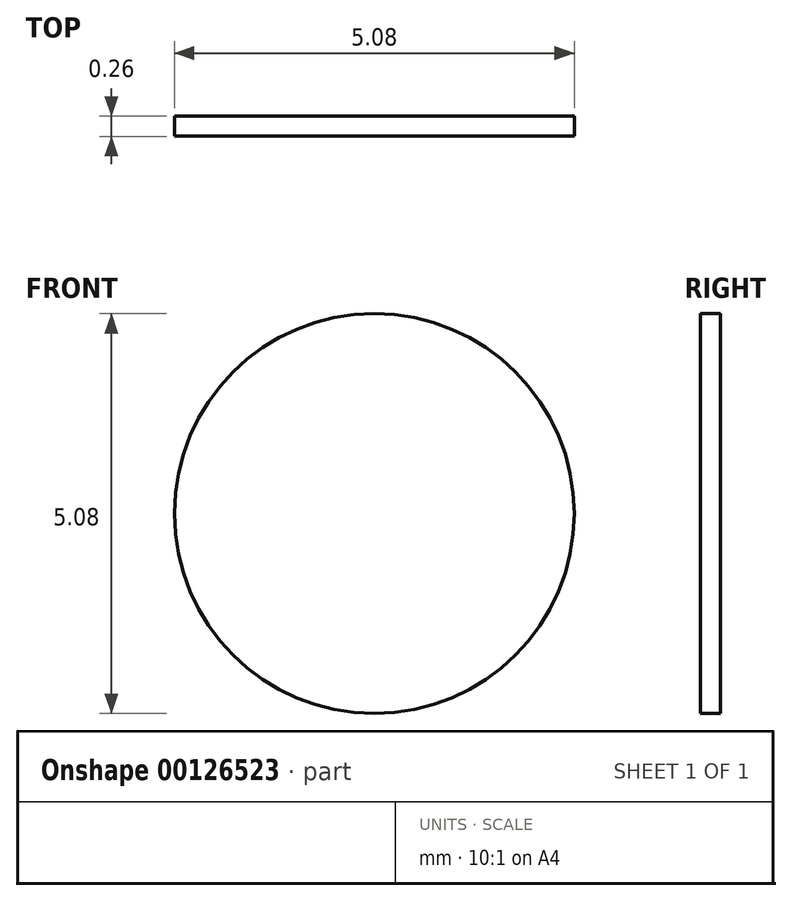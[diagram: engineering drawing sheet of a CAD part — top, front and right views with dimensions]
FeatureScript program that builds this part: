
annotation { "Feature Type Name" : "Feature", "Feature Type Description" : "" }
export const myFeature = defineFeature(function(context is Context, id is Id, definition is map)
    precondition{}
    {
        {
            var Q0;
            Q0=qCreatedBy(makeId("Front.planeOp"),FACE);
            var sketch = newSketch(context, id + "F0", { "sketchPlane" : qUnion([Q0])});
            skCircle(sketch, "E0", {"center": v(0, 0) * mm, "radius": 2.54 * mm});
            skSolve(sketch);
        }
        {
            var Q0;
            Q0=makeQuery(id+"F0.imprint","IMPRINT",FACE,{"disambiguationData":[TD([[makeQuery(id+"F0.imprint","IMPRINT",EDGE,{"derivedFrom":sQuery(id+"F0.wireOp",EDGE,"E0")}),1.0]])]});
            extrude(context, id + "F1", {"entities" : qUnion([Q0]), "endBound" : BoundingType.SYMMETRIC, "depth" : 0.25 * mm});
        }
    });
